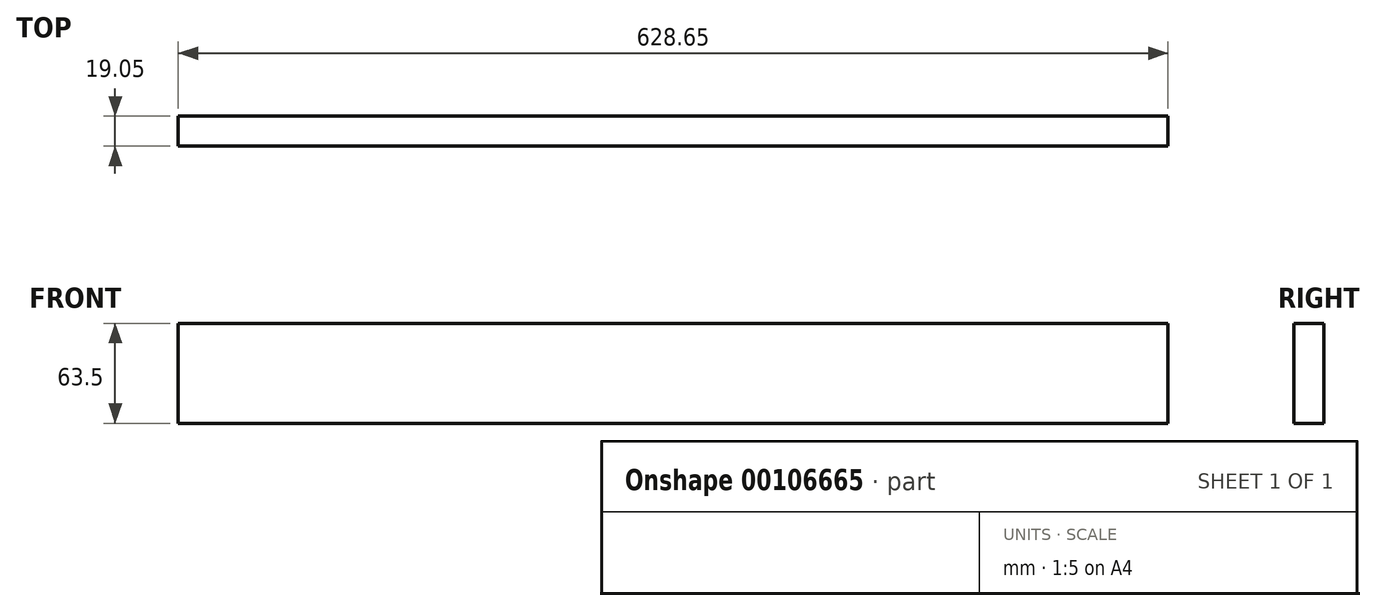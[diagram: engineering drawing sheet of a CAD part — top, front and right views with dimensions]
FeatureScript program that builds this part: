
annotation { "Feature Type Name" : "Feature", "Feature Type Description" : "" }
export const myFeature = defineFeature(function(context is Context, id is Id, definition is map)
    precondition{}
    {
        {
            var Q0;
            Q0=qCreatedBy(makeId("Front.planeOp"),FACE);
            var sketch = newSketch(context, id + "F0", { "sketchPlane" : qUnion([Q0])});
            skLineSegment(sketch, "E0.bottom", {"start": v(0, 0) * mm, "end": v(628.65, 0) * mm});
            skLineSegment(sketch, "E0.top", {"start": v(0, 63.5) * mm, "end": v(628.65, 63.5) * mm});
            skLineSegment(sketch, "E0.left", {"start": v(0, 0) * mm, "end": v(0, 63.5) * mm});
            skLineSegment(sketch, "E0.right", {"start": v(628.65, 0) * mm, "end": v(628.65, 63.5) * mm});
            skSolve(sketch);
        }
        {
            var Q0;
            Q0=makeQuery(id+"F0.imprint","IMPRINT",FACE,{"disambiguationData":[TD([[makeQuery(id+"F0.imprint","IMPRINT",EDGE,{"derivedFrom":sQuery(id+"F0.wireOp",EDGE,"E0.bottom")}),1.0]])]});
            extrude(context, id + "F1", {"entities" : qUnion([Q0]), "depth" : 19.05 * mm});
        }
    });
